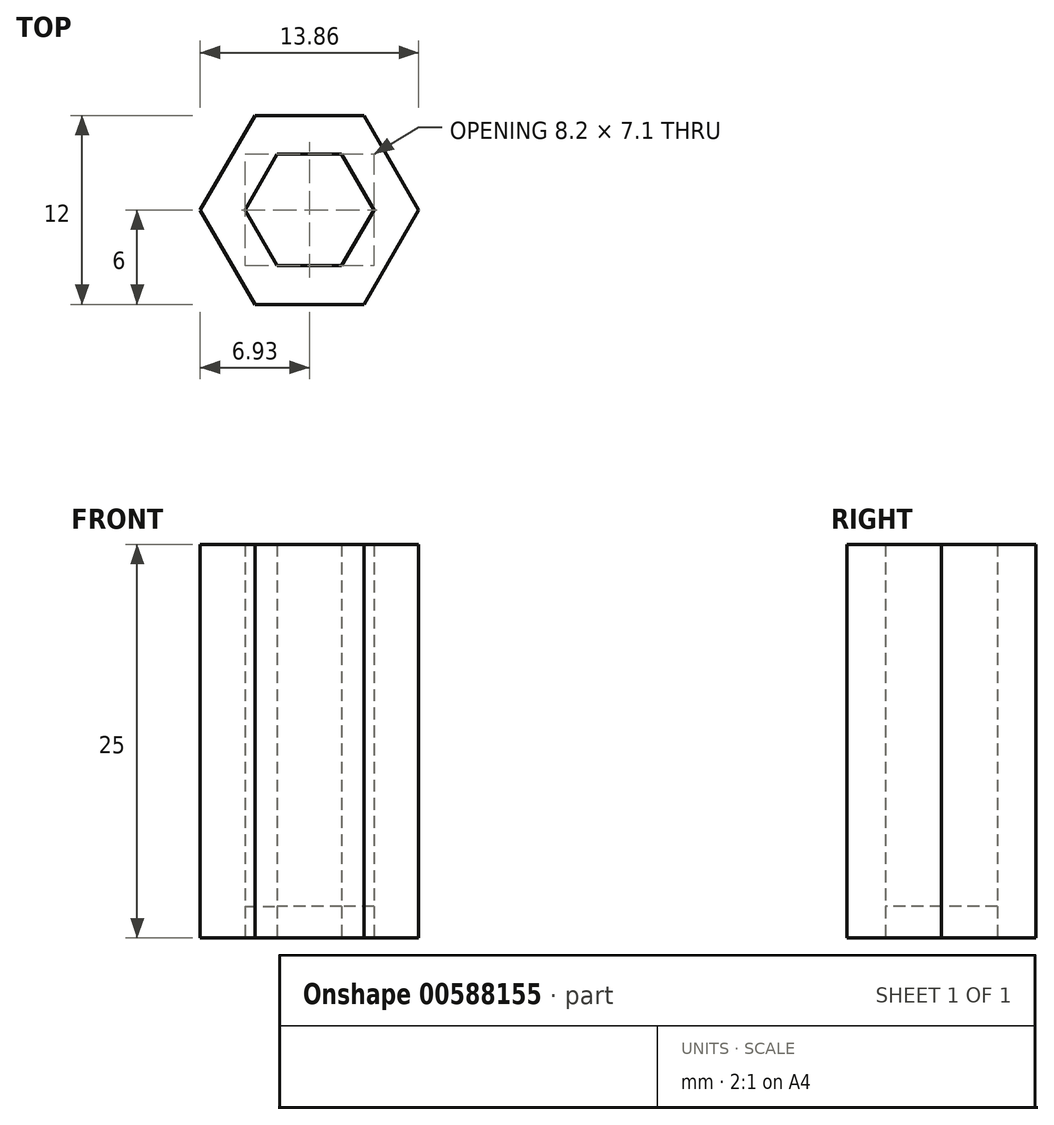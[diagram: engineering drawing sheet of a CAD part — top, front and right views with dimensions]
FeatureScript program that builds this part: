
annotation { "Feature Type Name" : "Feature", "Feature Type Description" : "" }
export const myFeature = defineFeature(function(context is Context, id is Id, definition is map)
    precondition{}
    {
        {
            var Q0;
            Q0=qCreatedBy(makeId("Top.planeOp"),FACE);
            var sketch = newSketch(context, id + "F0", { "sketchPlane" : qUnion([Q0])});
            skLineSegment(sketch, "E0.0", {"start": v(-2.05, 3.55) * mm, "end": v(2.05, 3.55) * mm});
            skLineSegment(sketch, "E0.1", {"start": v(2.05, 3.55) * mm, "end": v(4.1, 0) * mm});
            skLineSegment(sketch, "E0.2", {"start": v(4.1, 0) * mm, "end": v(2.05, -3.55) * mm});
            skLineSegment(sketch, "E0.3", {"start": v(2.05, -3.55) * mm, "end": v(-2.05, -3.55) * mm});
            skLineSegment(sketch, "E0.4", {"start": v(-2.05, -3.55) * mm, "end": v(-4.1, 0) * mm});
            skLineSegment(sketch, "E0.5", {"start": v(-4.1, 0) * mm, "end": v(-2.05, 3.55) * mm});
            skPoint(sketch, "E0.0.midPoint", {"position": v(0, 3.55) * mm});
            skPoint(sketch, "E1.0.midPoint", {"position": v(0, 4.05) * mm});
            skPoint(sketch, "E1.cCircle.center.orphan", {"position": v(0, 0) * mm});
            skPoint(sketch, "E2.orphan", {"position": v(-2.34, 4.05) * mm});
            skPoint(sketch, "E1.1.start.orphan", {"position": v(2.34, 4.05) * mm});
            skCircle(sketch, "E3.cCircle", {"center": v(0, 0) * mm, "radius": 6 * mm, "construction": true});
            skPoint(sketch, "E3.cCircle.perimeterSnap0", {"position": v(0, -3.55) * mm});
            skLineSegment(sketch, "E3.0", {"start": v(3.46, -6) * mm, "end": v(-3.46, -6) * mm});
            skLineSegment(sketch, "E3.1", {"start": v(-3.46, -6) * mm, "end": v(-6.93, 0) * mm});
            skLineSegment(sketch, "E3.2", {"start": v(-6.93, 0) * mm, "end": v(-3.46, 6) * mm});
            skLineSegment(sketch, "E3.3", {"start": v(-3.46, 6) * mm, "end": v(3.46, 6) * mm});
            skLineSegment(sketch, "E3.4", {"start": v(3.46, 6) * mm, "end": v(6.93, 0) * mm});
            skLineSegment(sketch, "E3.5", {"start": v(6.93, 0) * mm, "end": v(3.46, -6) * mm});
            skPoint(sketch, "E3.0.midPoint", {"position": v(0, -6) * mm});
            skPoint(sketch, "E3.0.midPoint.positionSnap0", {"position": v(0, -3.55) * mm});
            skSolve(sketch);
        }
        {
            var Q0;
            Q0 = qSketchRegion(id + "F0", true);
            extrude(context, id + "F1", {"entities" : qUnion([Q0]), "depth" : 25 * mm, "offsetDistance" : 25 * mm});
        }
        {
            var Q0;
            Q0=qCreatedBy(makeId("Top.planeOp"),FACE);
            var sketch = newSketch(context, id + "F2", { "sketchPlane" : qUnion([Q0])});
            skCircle(sketch, "E4.cCircle", {"center": v(0, 0) * mm, "radius": 3.55 * mm, "construction": true});
            skLineSegment(sketch, "E4.0", {"start": v(2.05, -3.55) * mm, "end": v(-2.05, -3.55) * mm});
            skLineSegment(sketch, "E4.1", {"start": v(-2.05, -3.55) * mm, "end": v(-4.1, 0) * mm});
            skLineSegment(sketch, "E4.2", {"start": v(-4.1, 0) * mm, "end": v(-2.05, 3.55) * mm});
            skLineSegment(sketch, "E4.3", {"start": v(-2.05, 3.55) * mm, "end": v(2.05, 3.55) * mm});
            skLineSegment(sketch, "E4.4", {"start": v(2.05, 3.55) * mm, "end": v(4.1, 0) * mm});
            skLineSegment(sketch, "E4.5", {"start": v(4.1, 0) * mm, "end": v(2.05, -3.55) * mm});
            skPoint(sketch, "E4.0.midPoint", {"position": v(0, -3.55) * mm});
            skSolve(sketch);
        }
        {
            var Q0;
            Q0 = qSketchRegion(id + "F2", true);
            extrude(context, id + "F3", {"entities" : qUnion([Q0]), "depth" : 2 * mm, "offsetDistance" : 25 * mm});
        }
    });
